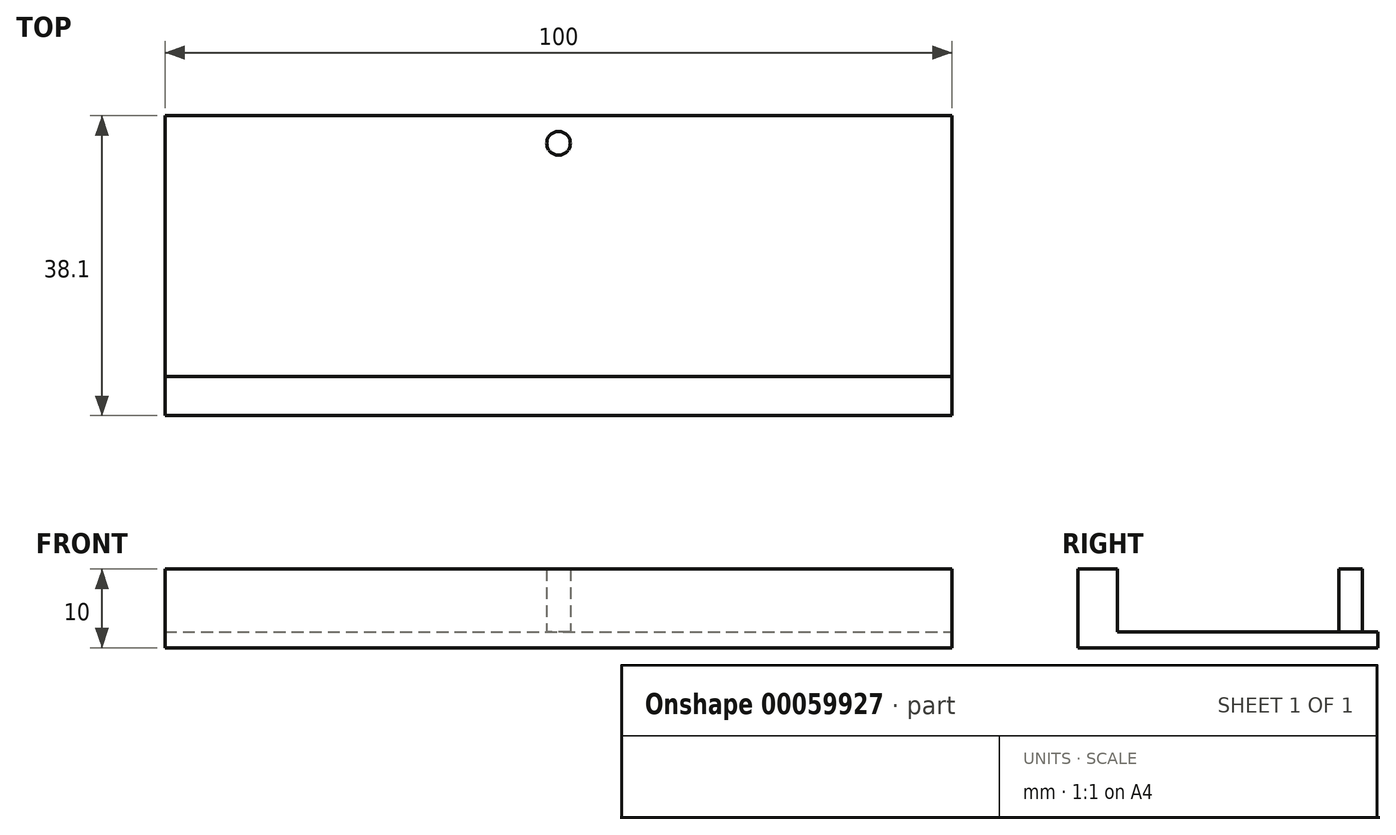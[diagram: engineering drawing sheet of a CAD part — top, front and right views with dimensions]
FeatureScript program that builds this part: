
annotation { "Feature Type Name" : "Feature", "Feature Type Description" : "" }
export const myFeature = defineFeature(function(context is Context, id is Id, definition is map)
    precondition{}
    {
        {
            var Q0;
            Q0=qCreatedBy(makeId("Top.planeOp"),FACE);
            var sketch = newSketch(context, id + "F0", { "sketchPlane" : qUnion([Q0])});
            skCircle(sketch, "E0", {"center": v(0, 29.6) * mm, "radius": 1.5 * mm});
            skLineSegment(sketch, "E1.bottom", {"start": v(-50, 0) * mm, "end": v(50, 0) * mm});
            skLineSegment(sketch, "E1.top", {"start": v(-50, -5) * mm, "end": v(50, -5) * mm});
            skLineSegment(sketch, "E1.left", {"start": v(-50, 0) * mm, "end": v(-50, -5) * mm});
            skLineSegment(sketch, "E1.right", {"start": v(50, 0) * mm, "end": v(50, -5) * mm});
            skSolve(sketch);
        }
        {
            var Q0;
            Q0 = qSketchRegion(id + "F0", true);
            extrude(context, id + "F1", {"entities" : qUnion([Q0]), "depth" : 10 * mm});
        }
        {
            var Q0;
            Q0=qCreatedBy(makeId("Top.planeOp"),FACE);
            var sketch = newSketch(context, id + "F2", { "sketchPlane" : qUnion([Q0])});
            skLineSegment(sketch, "E2.bottom", {"start": v(-50, -5) * mm, "end": v(50, -5) * mm});
            skLineSegment(sketch, "E2.top", {"start": v(-50, 33.1) * mm, "end": v(50, 33.1) * mm});
            skLineSegment(sketch, "E2.left", {"start": v(-50, -5) * mm, "end": v(-50, 33.1) * mm});
            skLineSegment(sketch, "E2.right", {"start": v(50, -5) * mm, "end": v(50, 33.1) * mm});
            skSolve(sketch);
        }
        {
            var Q0;
            Q0 = qSketchRegion(id + "F2", true);
            extrude(context, id + "F3", {"entities" : qUnion([Q0]), "operationType" : NewBodyOperationType.ADD, "depth" : 2 * mm});
        }
    });
